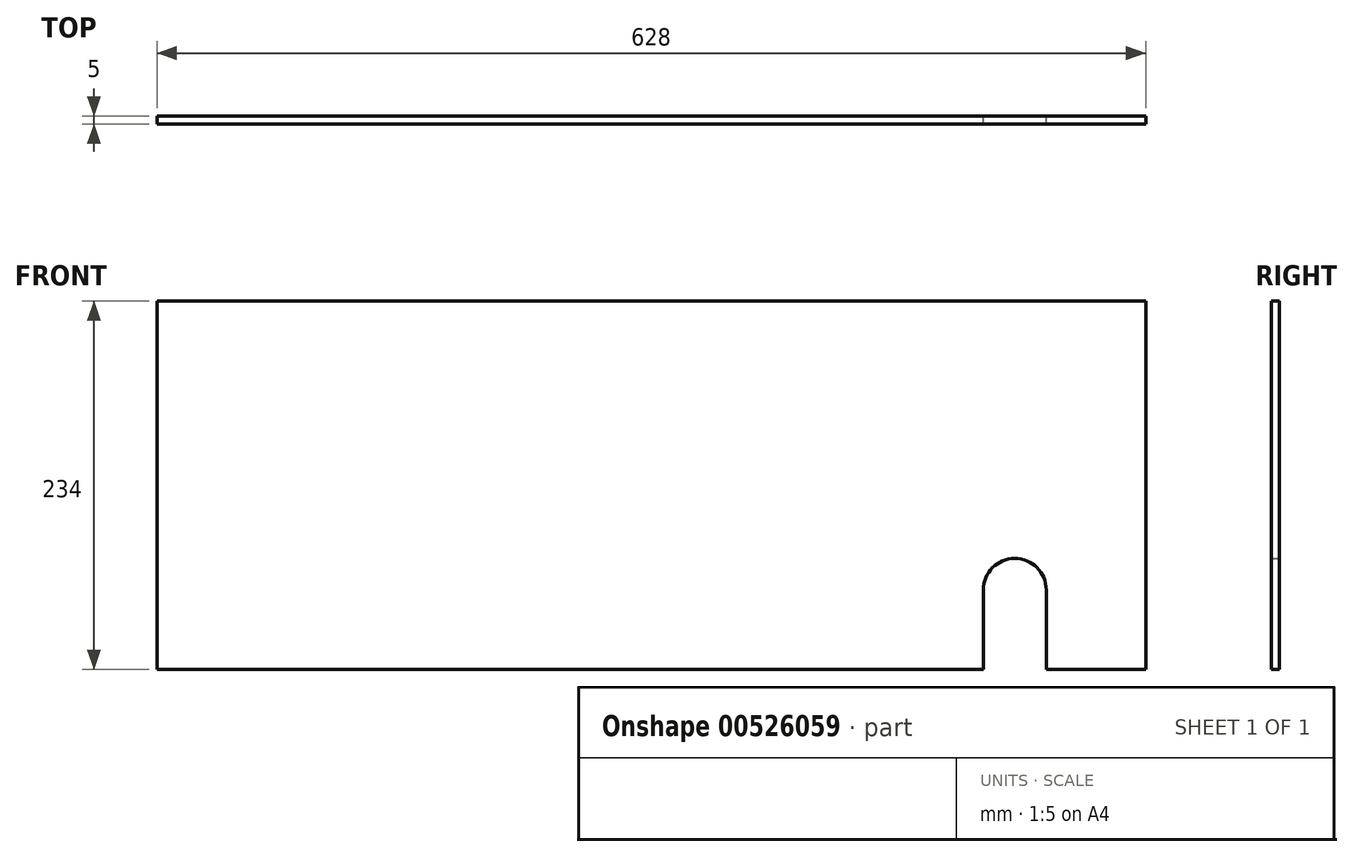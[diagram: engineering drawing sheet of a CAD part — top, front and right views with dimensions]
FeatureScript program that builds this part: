
annotation { "Feature Type Name" : "Feature", "Feature Type Description" : "" }
export const myFeature = defineFeature(function(context is Context, id is Id, definition is map)
    precondition{}
    {
        {
            var Q0;
            Q0=qCreatedBy(makeId("Front.planeOp"),FACE);
            var sketch = newSketch(context, id + "F0", { "sketchPlane" : qUnion([Q0])});
            skLineSegment(sketch, "E0.bottom", {"start": v(-592.56, 201.97) * mm, "end": v(35.44, 201.97) * mm});
            skLineSegment(sketch, "E0.top", {"start": v(-592.56, -32.03) * mm, "end": v(-67.66, -32.03) * mm});
            skArc(sketch, "E1", {"start": v(-27.66, 18.48) * mm, "mid": v(-47.66, 38.48) * mm, "end": v(-67.66, 18.48) * mm});
            skLineSegment(sketch, "E2", {"start": v(-27.66, 18.48) * mm, "end": v(-27.66, -32.03) * mm});
            skLineSegment(sketch, "E3", {"start": v(35.44, -32.03) * mm, "end": v(-27.66, -32.03) * mm});
            skLineSegment(sketch, "E4", {"start": v(-67.66, 18.48) * mm, "end": v(-67.66, -32.03) * mm});
            skLineSegment(sketch, "E5", {"start": v(-592.56, 201.97) * mm, "end": v(-592.56, -32.03) * mm});
            skLineSegment(sketch, "E6", {"start": v(35.44, 201.97) * mm, "end": v(35.44, -32.03) * mm});
            skLineSegment(sketch, "E7.trimOffspring", {"start": v(-27.66, -32.03) * mm, "end": v(35.44, -32.03) * mm});
            skSolve(sketch);
        }
        {
            var Q0;
            Q0=makeQuery(id+"F0.imprint","IMPRINT",FACE,{"disambiguationData":[TD([[makeQuery(id+"F0.imprint","IMPRINT",EDGE,{"derivedFrom":sQuery(id+"F0.wireOp",EDGE,"E0.bottom")}),-1.0]])]});
            extrude(context, id + "F1", {"entities" : qUnion([Q0]), "depth" : 5 * mm, "offsetDistance" : 25 * mm});
        }
    });
